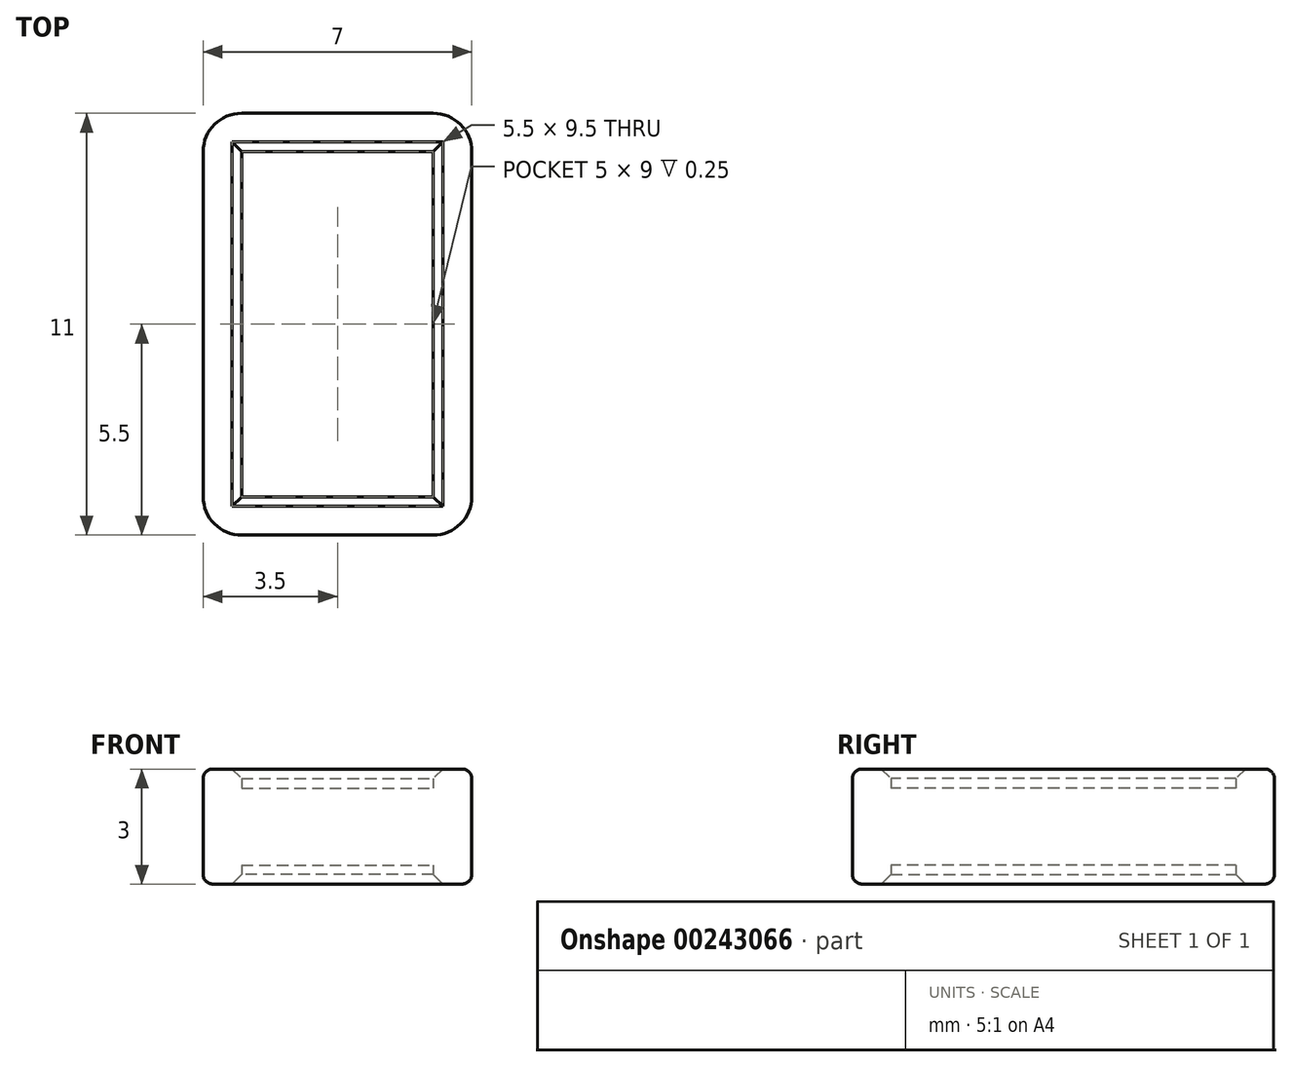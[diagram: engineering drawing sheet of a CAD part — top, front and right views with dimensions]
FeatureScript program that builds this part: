
annotation { "Feature Type Name" : "Feature", "Feature Type Description" : "" }
export const myFeature = defineFeature(function(context is Context, id is Id, definition is map)
    precondition{}
    {
        {
            var Q0;
            Q0=qCreatedBy(makeId("Top.planeOp"),FACE);
            var sketch = newSketch(context, id + "F0", { "sketchPlane" : qUnion([Q0])});
            skLineSegment(sketch, "E0", {"start": v(0, 0) * mm, "end": v(6, 0) * mm});
            skLineSegment(sketch, "E1", {"start": v(6, 0) * mm, "end": v(6, 10) * mm});
            skLineSegment(sketch, "E2", {"start": v(6, 10) * mm, "end": v(0, 10) * mm});
            skLineSegment(sketch, "E3", {"start": v(0, 10) * mm, "end": v(0, 0) * mm});
            skSolve(sketch);
        }
        {
            var Q0;
            Q0 = qSketchRegion(id + "F0", true);
            extrude(context, id + "F1", {"entities" : qUnion([Q0]), "depth" : 2 * mm});
        }
        {
            var Q0;
            Q0=makeQuery(id+"F1.opExtrude","SWEPT_EDGE",EDGE,{"disambiguationData":[OSD([sQuery(id+"F0.wireOp",EDGE,"E0"),sQuery(id+"F0.wireOp",EDGE,"E3")])]});
            var Q1;
            Q1=makeQuery(id+"F1.opExtrude","SWEPT_EDGE",EDGE,{"disambiguationData":[OSD([sQuery(id+"F0.wireOp",EDGE,"E0"),sQuery(id+"F0.wireOp",EDGE,"E1")])]});
            var Q2;
            Q2=makeQuery(id+"F1.opExtrude","SWEPT_EDGE",EDGE,{"disambiguationData":[OSD([sQuery(id+"F0.wireOp",EDGE,"E1"),sQuery(id+"F0.wireOp",EDGE,"E2")])]});
            var Q3;
            Q3=makeQuery(id+"F1.opExtrude","SWEPT_EDGE",EDGE,{"disambiguationData":[OSD([sQuery(id+"F0.wireOp",EDGE,"E2"),sQuery(id+"F0.wireOp",EDGE,"E3")])]});
            fillet(context, id + "F2", {"entities" : qUnion([Q0, Q1, Q2, Q3]), "radius" : 0.5 * mm, "tangentPropagation" : true, "allowEdgeOverflow" : false});
        }
        {
            var Q0;
            Q0=qCreatedBy(makeId("Front.planeOp"),FACE);
            cPlane(context, id + "F3", {"entities" : qUnion([Q0]), "cplaneType" : CPlaneType.OFFSET, "offset" : 0.5 * mm, "oppositeDirection" : true, "width" : 150 * mm, "height" : 150 * mm});
        }
        {
            var Q0;
            Q0=qCreatedBy(id+"F3.planeOp",FACE);
            var sketch = newSketch(context, id + "F4", { "sketchPlane" : qUnion([Q0])});
            skLineSegment(sketch, "E4.0", {"start": v(5.5, 2) * mm, "end": v(6, 2) * mm});
            skLineSegment(sketch, "E5.0", {"start": v(6, 2) * mm, "end": v(6, 0) * mm});
            skLineSegment(sketch, "E6.0", {"start": v(6, 0) * mm, "end": v(5.5, 0) * mm});
            skLineSegment(sketch, "E7.0", {"start": v(6.5, -0.5) * mm, "end": v(5.5, -0.5) * mm});
            skLineSegment(sketch, "E7.1", {"start": v(6.5, 2.5) * mm, "end": v(6.5, -0.5) * mm});
            skLineSegment(sketch, "E7.2", {"start": v(5.5, 2.5) * mm, "end": v(6.5, 2.5) * mm});
            skLineSegment(sketch, "E8", {"start": v(5.5, 2.5) * mm, "end": v(5.5, 2) * mm});
            skLineSegment(sketch, "E9", {"start": v(5.5, 0) * mm, "end": v(5.5, -0.5) * mm});
            skSolve(sketch);
        }
        {
            var Q0;
            Q0=makeQuery(id+"F1.opExtrude","CAP_FACE",FACE,{"disambiguationData":[OSD([sQuery(id+"F0.wireOp",EDGE,"E0"),sQuery(id+"F0.wireOp",EDGE,"E1"),sQuery(id+"F0.wireOp",EDGE,"E2"),sQuery(id+"F0.wireOp",EDGE,"E3")])],"isStart":false});
            var sketch = newSketch(context, id + "F5", { "sketchPlane" : qUnion([Q0])});
            skArc(sketch, "E10.0", {"start": v(0, 0.5) * mm, "mid": v(0.15, 0.15) * mm, "end": v(0.5, 0) * mm});
            skLineSegment(sketch, "E10.1", {"start": v(0.5, 0) * mm, "end": v(5.5, 0) * mm});
            skArc(sketch, "E10.2", {"start": v(5.5, 0) * mm, "mid": v(5.85, 0.15) * mm, "end": v(6, 0.5) * mm});
            skLineSegment(sketch, "E10.3", {"start": v(6, 0.5) * mm, "end": v(6, 9.5) * mm});
            skLineSegment(sketch, "E10.4", {"start": v(0, 9.5) * mm, "end": v(0, 0.5) * mm});
            skArc(sketch, "E10.5", {"start": v(0.5, 10) * mm, "mid": v(0.15, 9.85) * mm, "end": v(0, 9.5) * mm});
            skLineSegment(sketch, "E10.6", {"start": v(5.5, 10) * mm, "end": v(0.5, 10) * mm});
            skArc(sketch, "E10.7", {"start": v(6, 9.5) * mm, "mid": v(5.85, 9.85) * mm, "end": v(5.5, 10) * mm});
            skSolve(sketch);
        }
        {
            var Q0;
            Q0=makeQuery(id+"F4.imprint","IMPRINT",FACE,{"disambiguationData":[TD([[makeQuery(id+"F4.imprint","IMPRINT",EDGE,{"derivedFrom":sQuery(id+"F4.wireOp",EDGE,"E4.0")}),1.0]])]});
            var Q1;
            Q1=sQuery(id+"F5.wireOp",EDGE,"E10.3");
            var Q2;
            Q2=sQuery(id+"F5.wireOp",EDGE,"E10.2");
            var Q3;
            Q3=sQuery(id+"F5.wireOp",EDGE,"E10.1");
            var Q4;
            Q4=sQuery(id+"F5.wireOp",EDGE,"E10.0");
            var Q5;
            Q5=sQuery(id+"F5.wireOp",EDGE,"E10.4");
            var Q6;
            Q6=sQuery(id+"F5.wireOp",EDGE,"E10.6");
            var Q7;
            Q7=sQuery(id+"F5.wireOp",EDGE,"E10.5");
            var Q8;
            Q8=sQuery(id+"F5.wireOp",EDGE,"E10.7");
            sweep(context, id + "F6", {"operationType" : NewBodyOperationType.ADD, "profiles" : qUnion([Q0]), "path" : qUnion([Q1, Q2, Q3, Q4, Q5, Q6, Q7, Q8])});
        }
        {
            var Q0;
            Q0=makeQuery(id+"F6.opSweep","SWEPT_EDGE",EDGE,{"disambiguationData":[OSD([sQuery(id+"F4.wireOp",EDGE,"E7.1"),sQuery(id+"F4.wireOp",EDGE,"E7.2"),sQuery(id+"F5.wireOp",EDGE,"E10.3")])]});
            var Q1;
            Q1=makeQuery(id+"F6.opSweep","SWEPT_EDGE",EDGE,{"disambiguationData":[OSD([sQuery(id+"F4.wireOp",EDGE,"E7.1"),sQuery(id+"F4.wireOp",EDGE,"E7.2"),sQuery(id+"F5.wireOp",EDGE,"E10.2")])]});
            var Q2;
            Q2=makeQuery(id+"F6.opSweep","SWEPT_EDGE",EDGE,{"disambiguationData":[OSD([sQuery(id+"F4.wireOp",EDGE,"E7.1"),sQuery(id+"F4.wireOp",EDGE,"E7.2"),sQuery(id+"F5.wireOp",EDGE,"E10.1")])]});
            var Q3;
            Q3=makeQuery(id+"F6.opSweep","SWEPT_EDGE",EDGE,{"disambiguationData":[OSD([sQuery(id+"F4.wireOp",EDGE,"E7.0"),sQuery(id+"F4.wireOp",EDGE,"E7.1"),sQuery(id+"F5.wireOp",EDGE,"E10.3")])]});
            fillet(context, id + "F7", {"entities" : qUnion([Q0, Q1, Q2, Q3]), "radius" : 0.25 * mm, "tangentPropagation" : true, "allowEdgeOverflow" : false});
        }
        {
            var Q0;
            Q0=makeQuery(id+"F6.opSweep","SWEPT_EDGE",EDGE,{"disambiguationData":[OSD([sQuery(id+"F4.wireOp",EDGE,"E7.2"),sQuery(id+"F4.wireOp",EDGE,"E8"),sQuery(id+"F5.wireOp",EDGE,"E10.4")])]});
            var Q1;
            Q1=makeQuery(id+"F6.opSweep","SWEPT_EDGE",EDGE,{"disambiguationData":[OSD([sQuery(id+"F4.wireOp",EDGE,"E7.2"),sQuery(id+"F4.wireOp",EDGE,"E8"),sQuery(id+"F5.wireOp",EDGE,"E10.6")])]});
            var Q2;
            Q2=makeQuery(id+"F6.opSweep","SWEPT_EDGE",EDGE,{"disambiguationData":[OSD([sQuery(id+"F4.wireOp",EDGE,"E7.2"),sQuery(id+"F4.wireOp",EDGE,"E8"),sQuery(id+"F5.wireOp",EDGE,"E10.3")])]});
            var Q3;
            Q3=makeQuery(id+"F6.opSweep","SWEPT_EDGE",EDGE,{"disambiguationData":[OSD([sQuery(id+"F4.wireOp",EDGE,"E7.2"),sQuery(id+"F4.wireOp",EDGE,"E8"),sQuery(id+"F5.wireOp",EDGE,"E10.1")])]});
            var Q4;
            Q4=makeQuery(id+"F6.opSweep","SWEPT_EDGE",EDGE,{"disambiguationData":[OSD([sQuery(id+"F4.wireOp",EDGE,"E7.0"),sQuery(id+"F4.wireOp",EDGE,"E9"),sQuery(id+"F5.wireOp",EDGE,"E10.4")])]});
            var Q5;
            Q5=makeQuery(id+"F6.opSweep","SWEPT_EDGE",EDGE,{"disambiguationData":[OSD([sQuery(id+"F4.wireOp",EDGE,"E7.0"),sQuery(id+"F4.wireOp",EDGE,"E9"),sQuery(id+"F5.wireOp",EDGE,"E10.1")])]});
            var Q6;
            Q6=makeQuery(id+"F6.opSweep","SWEPT_EDGE",EDGE,{"disambiguationData":[OSD([sQuery(id+"F4.wireOp",EDGE,"E7.0"),sQuery(id+"F4.wireOp",EDGE,"E9"),sQuery(id+"F5.wireOp",EDGE,"E10.3")])]});
            var Q7;
            Q7=makeQuery(id+"F6.opSweep","SWEPT_EDGE",EDGE,{"disambiguationData":[OSD([sQuery(id+"F4.wireOp",EDGE,"E7.0"),sQuery(id+"F4.wireOp",EDGE,"E9"),sQuery(id+"F5.wireOp",EDGE,"E10.6")])]});
            chamfer(context, id + "F8", {"entities" : qUnion([Q0, Q1, Q2, Q3, Q4, Q5, Q6, Q7]), "width" : 0.25 * mm, "tangentPropagation" : true});
        }
    });
